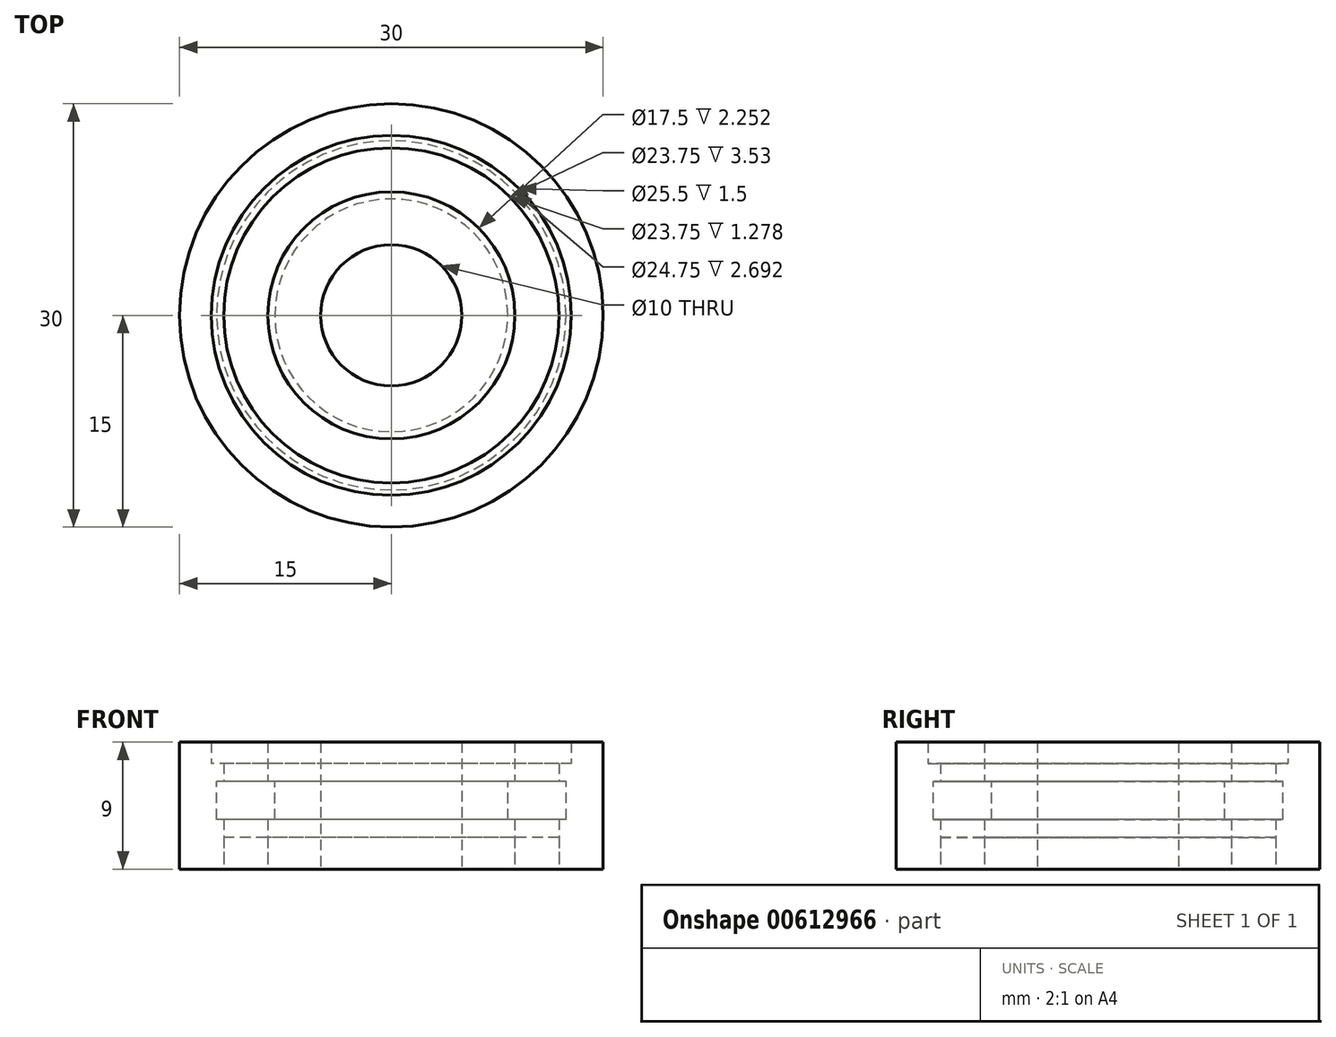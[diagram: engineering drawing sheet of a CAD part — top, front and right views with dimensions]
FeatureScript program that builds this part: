
annotation { "Feature Type Name" : "Feature", "Feature Type Description" : "" }
export const myFeature = defineFeature(function(context is Context, id is Id, definition is map)
    precondition{}
    {
        {
            var Q0;
            Q0=qCreatedBy(makeId("Top.planeOp"),FACE);
            var sketch = newSketch(context, id + "F0", { "sketchPlane" : qUnion([Q0])});
            skCircle(sketch, "E0", {"center": v(0, 0) * mm, "radius": 15 * mm});
            skCircle(sketch, "E1", {"center": v(0, 0) * mm, "radius": 5 * mm});
            skCircle(sketch, "E2", {"center": v(0, 0) * mm, "radius": 12.75 * mm});
            skCircle(sketch, "E3", {"center": v(0, 0) * mm, "radius": 11.88 * mm});
            skCircle(sketch, "E4", {"center": v(0, 0) * mm, "radius": 8.75 * mm});
            skSolve(sketch);
        }
        {
            var Q0;
            Q0=makeQuery(id+"F0.imprint","IMPRINT",FACE,{"disambiguationData":[TD([[makeQuery(id+"F0.imprint","IMPRINT",EDGE,{"derivedFrom":sQuery(id+"F0.wireOp",EDGE,"E0")}),1.0]])]});
            var Q1;
            Q1=makeQuery(id+"F0.imprint","IMPRINT",FACE,{"disambiguationData":[TD([[makeQuery(id+"F0.imprint","IMPRINT",EDGE,{"derivedFrom":sQuery(id+"F0.wireOp",EDGE,"E1")}),-1.0]])]});
            extrude(context, id + "F1", {"entities" : qUnion([Q0, Q1]), "depth" : 9 * mm, "offsetDistance" : 25 * mm});
        }
        {
            var Q0;
            Q0=makeQuery(id+"F0.imprint","IMPRINT",FACE,{"disambiguationData":[TD([[makeQuery(id+"F0.imprint","IMPRINT",EDGE,{"derivedFrom":sQuery(id+"F0.wireOp",EDGE,"E2")}),1.0]])]});
            extrude(context, id + "F2", {"entities" : qUnion([Q0]), "operationType" : NewBodyOperationType.ADD, "depth" : 7.5 * mm, "offsetDistance" : 25 * mm});
        }
        {
            var Q0;
            Q0=makeQuery(id+"F0.imprint","IMPRINT",FACE,{"disambiguationData":[TD([[makeQuery(id+"F0.imprint","IMPRINT",EDGE,{"derivedFrom":sQuery(id+"F0.wireOp",EDGE,"E3")}),1.0]])]});
            extrude(context, id + "F3", {"entities" : qUnion([Q0]), "depth" : 2.25 * mm, "offsetDistance" : 25 * mm});
        }
        {
            var Q0;
            Q0=makeQuery(id+"F2.opExtrude","CAP_FACE",FACE,{"disambiguationData":[OSD([sQuery(id+"F0.wireOp",EDGE,"E2"),sQuery(id+"F0.wireOp",EDGE,"E3")])],"isStart":false});
            var sketch = newSketch(context, id + "F4", { "sketchPlane" : qUnion([Q0])});
            skLineSegment(sketch, "E5", {"start": v(0, 11.88) * mm, "end": v(0, 0) * mm});
            skCircle(sketch, "E6", {"center": v(0, 0) * mm, "radius": 12.38 * mm});
            skSolve(sketch);
        }
        {
            var Q0;
            Q0=makeQuery(id+"F4.imprint","IMPRINT",FACE,{"disambiguationData":[TD([[makeQuery(id+"F4.imprint","IMPRINT",EDGE,{"derivedFrom":sQuery(id+"F4.wireOp",EDGE,"E6")}),1.0]])]});
            extrude(context, id + "F5", {"entities" : qUnion([Q0]), "operationType" : NewBodyOperationType.REMOVE, "oppositeDirection" : true, "depth" : 3.97 * mm, "offsetDistance" : 25 * mm, "hasSecondDirection" : true, "secondDirectionOppositeDirection" : true, "secondDirectionDepth" : 1.28 * mm});
        }
        {
            var Q0;
            Q0=makeQuery(id+"F1.opExtrude","CAP_FACE",FACE,{"disambiguationData":[OSD([sQuery(id+"F0.wireOp",EDGE,"E1"),sQuery(id+"F0.wireOp",EDGE,"E4")])],"isStart":false});
            var sketch = newSketch(context, id + "F6", { "sketchPlane" : qUnion([Q0])});
            skLineSegment(sketch, "E7", {"start": v(0, 8.75) * mm, "end": v(0, 0) * mm});
            skCircle(sketch, "E8", {"center": v(0, 0) * mm, "radius": 8.25 * mm});
            skSolve(sketch);
        }
        {
            var Q0;
            Q0=makeQuery(id+"F6.imprint","IMPRINT",FACE,{"disambiguationData":[TD([[makeQuery(id+"F6.imprint","IMPRINT",EDGE,{"derivedFrom":sQuery(id+"F6.wireOp",EDGE,"E8")}),-1.0]])]});
            extrude(context, id + "F7", {"entities" : qUnion([Q0]), "operationType" : NewBodyOperationType.REMOVE, "oppositeDirection" : true, "depth" : 5.48 * mm, "offsetDistance" : 25 * mm, "hasSecondDirection" : true, "secondDirectionOppositeDirection" : true, "secondDirectionDepth" : 2.8 * mm});
        }
    });
